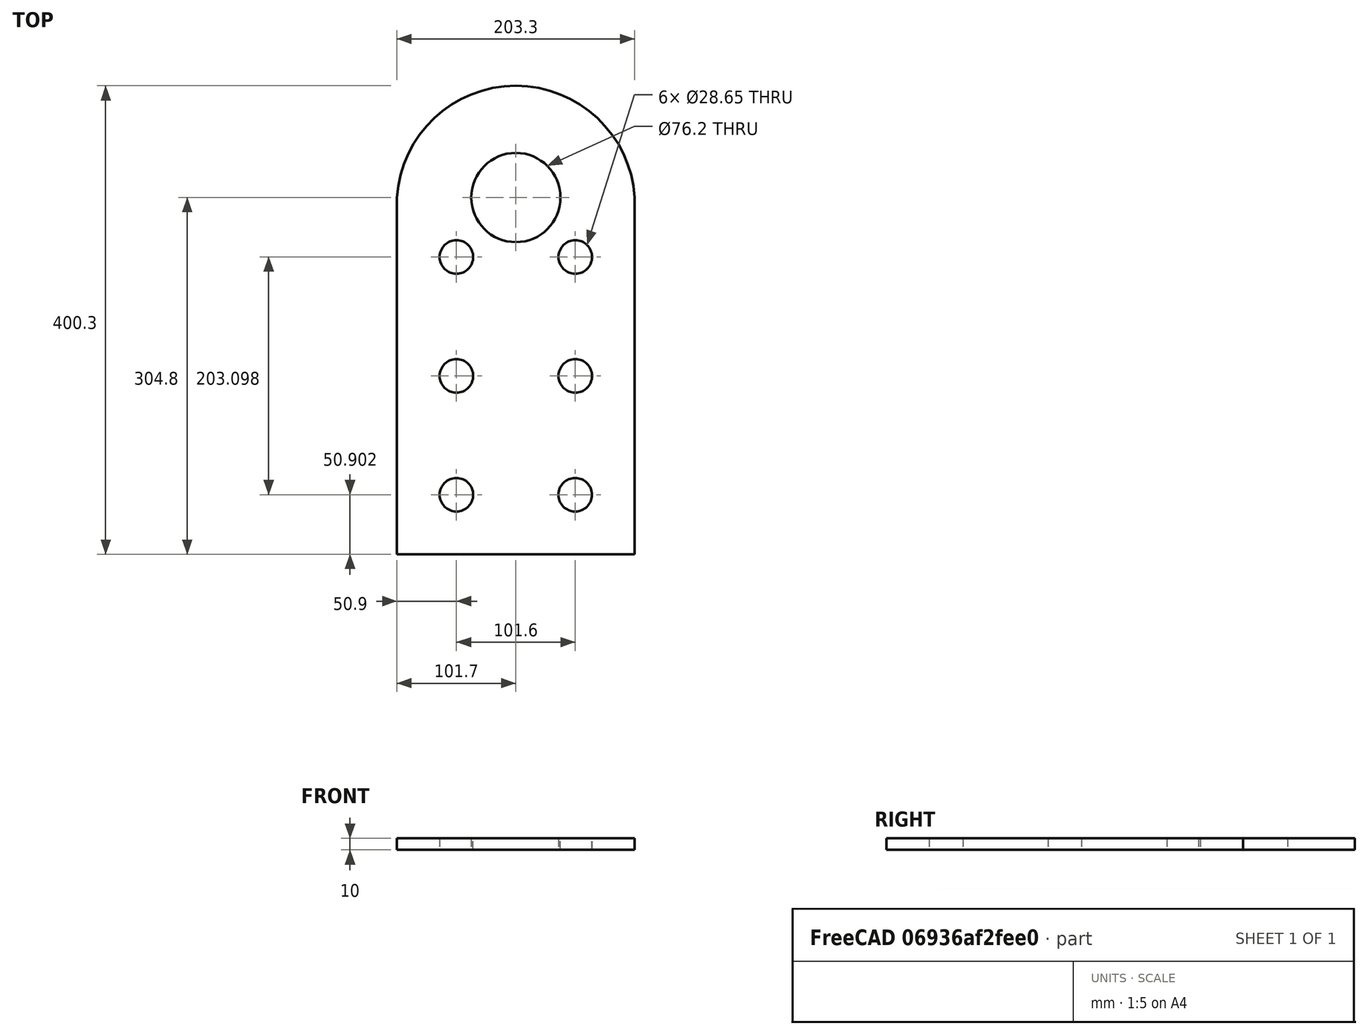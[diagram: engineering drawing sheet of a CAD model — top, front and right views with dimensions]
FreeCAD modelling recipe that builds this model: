
FCSTD DOCUMENT  (FreeCAD 0.16R6702 (Git))
Label: Pivot Plate
License: All rights reserved
LicenseURL: http://en.wikipedia.org/wiki/All_rights_reserved
objects: Sketcher::SketchObject×1, PartDesign::Pad×1
note: 3 computed .brp shape members not serialized (recipe doc carries the construction recipe); baked Part::Feature solids carry a one-line shape summary decoded from their .brp

FEATURE [Sketcher::SketchObject] Sketch
  sketch-geometry (11):
    g0: LineSegment StartX=0 StartY=304.8 StartZ=0 EndX=0 EndY=0 EndZ=0
    g1: LineSegment StartX=0 StartY=0 StartZ=0 EndX=-203.302 EndY=0 EndZ=0
    g2: LineSegment StartX=-203.302 StartY=0 StartZ=0 EndX=-203.302 EndY=304.8 EndZ=0
    g3: ArcOfCircle CenterX=-101.651 CenterY=298.45 CenterZ=0 NormalX=0 NormalY=0 NormalZ=1 Radius=101.849 StartAngle=0.0623877 EndAngle=3.0792
    g4: Circle CenterX=-152.4 CenterY=50.9016 CenterZ=0 NormalX=0 NormalY=0 NormalZ=1 Radius=14.3256
    g5: Circle CenterX=-50.9016 CenterY=50.9016 CenterZ=0 NormalX=0 NormalY=0 NormalZ=1 Radius=14.3256
    g6: Circle CenterX=-152.4 CenterY=152.4 CenterZ=0 NormalX=0 NormalY=0 NormalZ=1 Radius=14.3256
    g7: Circle CenterX=-50.8 CenterY=152.4 CenterZ=0 NormalX=0 NormalY=0 NormalZ=1 Radius=14.3256
    g8: Circle CenterX=-152.4 CenterY=254 CenterZ=0 NormalX=0 NormalY=0 NormalZ=1 Radius=14.3256
    g9: Circle CenterX=-50.8 CenterY=254 CenterZ=0 NormalX=0 NormalY=0 NormalZ=1 Radius=14.3256
    g10: Circle CenterX=-101.6 CenterY=304.8 CenterZ=0 NormalX=0 NormalY=0 NormalZ=1 Radius=38.1
  constraints (19):
    c: Coincident(g0,g1)
    c: Coincident(g1,g2)
    c: Horizontal(g1)
    c: Vertical(g0)
    c: Vertical(g2)
    c: Coincident(g0,g-1)
    c: DistanceY(g2,g2) = 304.8
    c: DistanceX(g1,g1) = 203.302
    c: DistanceY(g-1,g3) = 298.45
    c: Radius(g4) = 14.3256
    c: DistanceX(g1,g4) = 50.9016
    c: DistanceY(g1,g4) = 50.9016
    c: Equal(g4,g5) = 14.3256
    c: DistanceX(g5,g-1) = 50.9016
    c: DistanceY(g-1,g5) = 50.9016
    c: Equal(g4,g6) = 14.3256
    c: DistanceY(g4,g6) = 101.498
    c: DistanceX(g1,g6) = 50.9016
    c: Radius(g10) = 38.1
FEATURE [PartDesign::Pad] Pad
  Length = 10
  Length2 = 100
  Sketch = -> Sketch
  Type = 0
